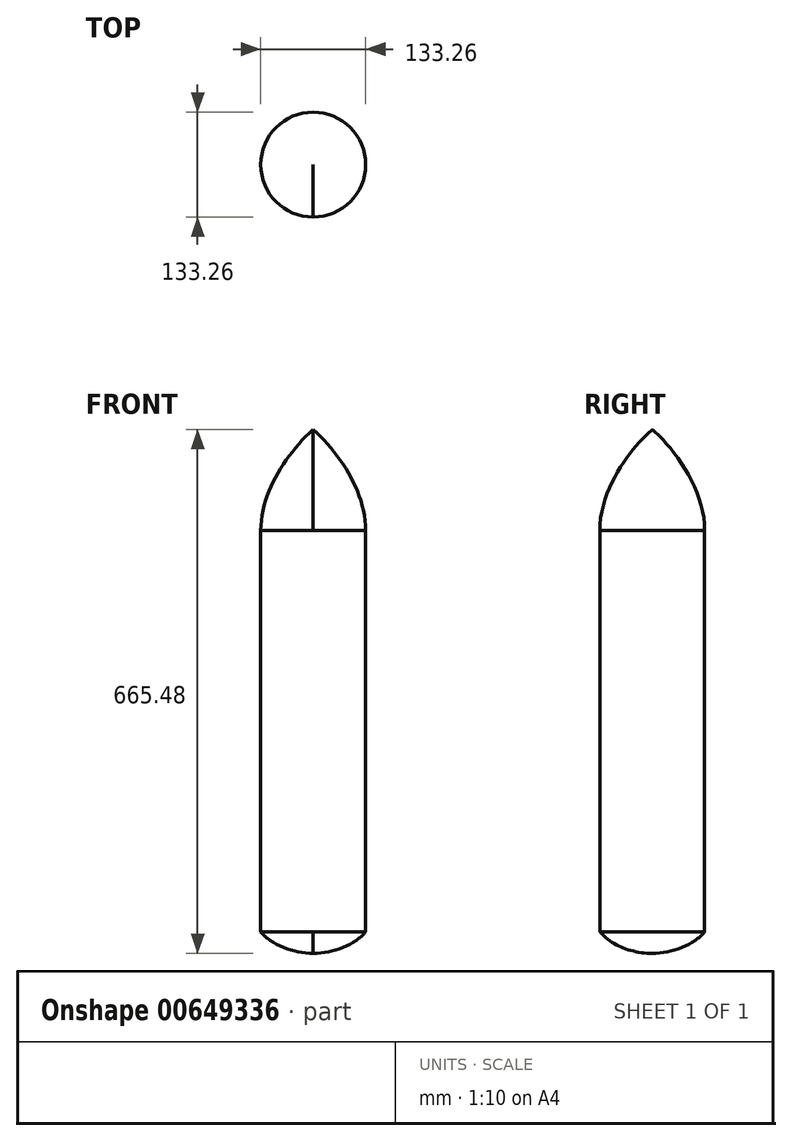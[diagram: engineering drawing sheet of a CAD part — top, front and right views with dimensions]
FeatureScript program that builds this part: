
annotation { "Feature Type Name" : "Feature", "Feature Type Description" : "" }
export const myFeature = defineFeature(function(context is Context, id is Id, definition is map)
    precondition{}
    {
        {
            var Q0;
            Q0=qCreatedBy(makeId("Top.planeOp"),FACE);
            var sketch = newSketch(context, id + "F0", { "sketchPlane" : qUnion([Q0])});
            skCircle(sketch, "E0", {"center": v(0, 0) * mm, "radius": 66.63 * mm});
            skLineSegment(sketch, "E1", {"start": v(0, 66.63) * mm, "end": v(0, -66.63) * mm});
            skLineSegment(sketch, "E2", {"start": v(0, 0) * mm, "end": v(-66.63, 0) * mm});
            skSolve(sketch);
        }
        {
            var Q0;
            {var subQ3=sQuery(id+"F0.wireOp",EDGE,"E2");Q0=makeQuery(id+"F0.imprint","IMPRINT",FACE,{"disambiguationData":[TD([[makeQuery(id+"F0.imprint","IMPRINT",EDGE,{"derivedFrom":subQ3}),1.0]])]});}
            extrude(context, id + "F1", {"entities" : qUnion([Q0]), "endBound" : BoundingType.SYMMETRIC, "depth" : 497.84 * mm, "offsetDistance" : 25.4 * mm});
        }
        {
            var Q0;
            Q0=makeQuery(id+"F1.opExtrude","CAP_FACE",FACE,{"disambiguationData":[OSD([sQuery(id+"F0.wireOp",EDGE,"E0")])],"isStart":false});
            extrude(context, id + "F2", {"entities" : qUnion([Q0]), "operationType" : NewBodyOperationType.ADD, "depth" : 124.46 * mm, "offsetDistance" : 25.4 * mm});
        }
        {
            var Q0;
            Q0=makeQuery(id+"F1.opExtrude","CAP_FACE",FACE,{"disambiguationData":[OSD([sQuery(id+"F0.wireOp",EDGE,"E0")])],"isStart":true});
            extrude(context, id + "F3", {"entities" : qUnion([Q0]), "operationType" : NewBodyOperationType.ADD, "depth" : 43.18 * mm, "offsetDistance" : 25.4 * mm});
        }
        {
            var Q0;
            {var subQ0=sQuery(id+"F0.wireOp",EDGE,"E1");Q0=makeQuery(id+"F3.boolean.opBoolean","MERGE",FACE,{"derivedFrom":[makeQuery(id+"F2.boolean.opBoolean","MERGE",FACE,{"derivedFrom":[makeQuery(id+"F1.opExtrude","SWEPT_FACE",FACE,{"disambiguationData":[OSD([subQ0])]}),makeQuery(id+"F2.opExtrude","SWEPT_FACE",FACE,{"disambiguationData":[OSD([subQ0])]})]}),makeQuery(id+"F3.opExtrude","SWEPT_FACE",FACE,{"disambiguationData":[OSD([subQ0])]})]});}
            var sketch = newSketch(context, id + "F4", { "sketchPlane" : qUnion([Q0])});
            skFitSpline(sketch, "E3", {"points": [v(0, 373.38) * mm, v(-66.63, 244.88) * mm], "startDerivative": vector(-38.7, -30.27) * mm, "endDerivative": vector(0, -189.73) * mm});
            skFitSpline(sketch, "E4", {"points": [v(0, -292.1) * mm, v(-66.63, -264.74) * mm], "startDerivative": vector(-81.09, 0) * mm, "endDerivative": vector(-40.1, 47.87) * mm});
            skSolve(sketch);
        }
        {
            var Q0;
            {var subQ0=sQuery(id+"F4.wireOp",EDGE,"E3");Q0=makeQuery(id+"F4.imprint","IMPRINT",FACE,{"disambiguationData":[TD([[makeQuery(id+"F4.imprint","IMPRINT",EDGE,{"derivedFrom":subQ0}),-1.0]])]});}
            extrude(context, id + "F5", {"entities" : qUnion([Q0]), "operationType" : NewBodyOperationType.ADD, "depth" : 0 * mm, "offsetDistance" : 25.4 * mm});
        }
        {
            var Q0;
            {var subQ0=sQuery(id+"F4.wireOp",EDGE,"E4");Q0=makeQuery(id+"F4.imprint","IMPRINT",FACE,{"disambiguationData":[TD([[makeQuery(id+"F4.imprint","IMPRINT",EDGE,{"derivedFrom":subQ0}),1.0]])]});}
            extrude(context, id + "F6", {"entities" : qUnion([Q0]), "operationType" : NewBodyOperationType.ADD, "depth" : 0 * mm, "offsetDistance" : 25.4 * mm});
        }
        {
            var Q0;
            {var subQ0=sQuery(id+"F4.wireOp",EDGE,"E3");Q0=makeQuery(id+"F4.imprint","IMPRINT",FACE,{"disambiguationData":[TD([[makeQuery(id+"F4.imprint","IMPRINT",EDGE,{"derivedFrom":subQ0}),-1.0]])]});}
            var Q1;
            {var subQ0=sQuery(id+"F4.wireOp",EDGE,"E4");Q1=makeQuery(id+"F4.imprint","IMPRINT",FACE,{"disambiguationData":[TD([[makeQuery(id+"F4.imprint","IMPRINT",EDGE,{"derivedFrom":subQ0}),1.0]])]});}
            var Q2;
            Q2=sQuery(id+"F4.wireOp",EDGE,"E3");
            var Q3;
            Q3=sQuery(id+"F4.wireOp",EDGE,"E4");
            var Q4;
            {var subQ0=sQuery(id+"F0.wireOp",EDGE,"E1");var subQ1=sQuery(id+"F0.wireOp",EDGE,"E0");Q4=makeQuery(id+"F6.boolean.opBoolean","SPLIT",EDGE,{"derivedFrom":makeQuery(id+"F5.boolean.opBoolean","SPLIT",EDGE,{"derivedFrom":makeQuery(id+"F3.boolean.opBoolean","MERGE",EDGE,{"derivedFrom":[makeQuery(id+"F2.boolean.opBoolean","MERGE",EDGE,{"derivedFrom":[makeQuery(id+"F1.opExtrude","SWEPT_EDGE",EDGE,{"disambiguationData":[OSD([subQ1,subQ0])]}),makeQuery(id+"F2.opExtrude","SWEPT_EDGE",EDGE,{"disambiguationData":[OSD([subQ1,subQ0])]})]}),makeQuery(id+"F3.opExtrude","SWEPT_EDGE",EDGE,{"disambiguationData":[OSD([subQ1,subQ0])]})]})})});}
            var Q5;
            {var subQ0=sQuery(id+"F0.wireOp",EDGE,"E2");var subQ1=sQuery(id+"F0.wireOp",EDGE,"E1");Q5=makeQuery(id+"F3.boolean.opBoolean","MERGE",EDGE,{"derivedFrom":[makeQuery(id+"F2.boolean.opBoolean","MERGE",EDGE,{"derivedFrom":[makeQuery(id+"F1.opExtrude","SWEPT_EDGE",EDGE,{"disambiguationData":[OSD([subQ1,subQ0])]}),makeQuery(id+"F2.opExtrude","SWEPT_EDGE",EDGE,{"disambiguationData":[OSD([subQ1,subQ0])]})]}),makeQuery(id+"F3.opExtrude","SWEPT_EDGE",EDGE,{"disambiguationData":[OSD([subQ1,subQ0])]})]});}
            revolve(context, id + "F7", {"bodyType" : ToolBodyType.SURFACE, "operationType" : NewBodyOperationType.REMOVE, "entities" : qUnion([Q0, Q1]), "surfaceEntities" : qUnion([Q2, Q3, Q4]), "axis" : qUnion([Q5]), "revolveType" : RevolveType.FULL, "oppositeDirection" : true});
        }
        {
            var Q0;
            {var subQ0=sQuery(id+"F0.wireOp",EDGE,"E1");Q0=makeQuery(id+"F5.boolean.opBoolean","MERGE",FACE,{"derivedFrom":[makeQuery(id+"F2.opExtrude","CAP_FACE",FACE,{"disambiguationData":[OSD([sQuery(id+"F0.wireOp",EDGE,"E0"),subQ0,sQuery(id+"F0.wireOp",EDGE,"E2")])],"isStart":false}),makeQuery(id+"F5.opExtrude","SWEPT_FACE",FACE,{"disambiguationData":[OSD([subQ0])]})]});}
            extrude(context, id + "F8", {"entities" : qUnion([Q0]), "operationType" : NewBodyOperationType.REMOVE, "oppositeDirection" : true, "depth" : 695.96 * mm, "offsetDistance" : 25.4 * mm});
        }
    });
